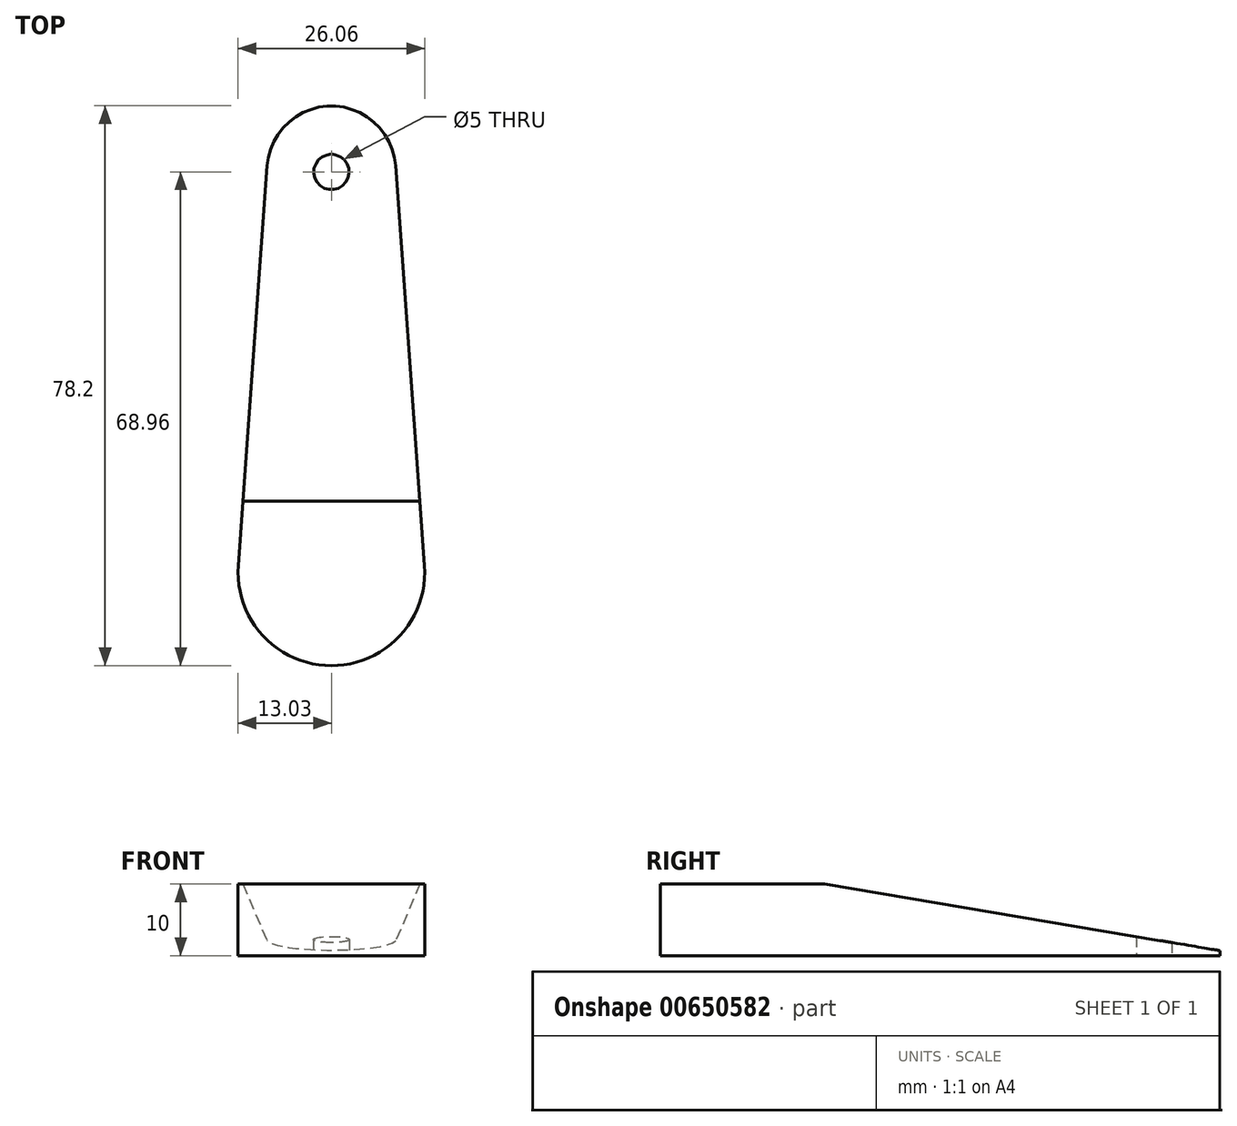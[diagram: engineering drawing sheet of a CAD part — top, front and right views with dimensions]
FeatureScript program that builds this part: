
annotation { "Feature Type Name" : "Feature", "Feature Type Description" : "" }
export const myFeature = defineFeature(function(context is Context, id is Id, definition is map)
    precondition{}
    {
        {
            var Q0;
            Q0=qCreatedBy(makeId("Top.planeOp"),FACE);
            var sketch = newSketch(context, id + "F0", { "sketchPlane" : qUnion([Q0])});
            skLineSegment(sketch, "E0", {"start": v(13, 0) * mm, "end": v(9, 55.86) * mm});
            skLineSegment(sketch, "E1", {"start": v(-13, 0) * mm, "end": v(-9, 55.86) * mm});
            skArc(sketch, "E2", {"start": v(-13, 0) * mm, "mid": v(0, -13.96) * mm, "end": v(13, 0) * mm});
            skArc(sketch, "E3", {"start": v(9, 55.86) * mm, "mid": v(0, 64.24) * mm, "end": v(-9, 55.86) * mm});
            skCircle(sketch, "E4", {"center": v(0, 55) * mm, "radius": 2.5 * mm});
            skPoint(sketch, "E5", {"position": v(0, 0) * mm});
            skSolve(sketch);
        }
        {
            var Q0;
            Q0 = qSketchRegion(id + "F0", true);
            extrude(context, id + "F1", {"entities" : qUnion([Q0]), "depth" : 10 * mm, "offsetDistance" : 25 * mm});
        }
        {
            var Q0;
            Q0=qCreatedBy(makeId("Right.planeOp"),FACE);
            var sketch = newSketch(context, id + "F2", { "sketchPlane" : qUnion([Q0])});
            skLineSegment(sketch, "E6", {"start": v(9, 10) * mm, "end": v(68.33, 0) * mm});
            skLineSegment(sketch, "E7", {"start": v(9, 10) * mm, "end": v(68.33, 10) * mm});
            skLineSegment(sketch, "E8", {"start": v(68.33, 0) * mm, "end": v(68.33, 10) * mm});
            skSolve(sketch);
        }
        {
            var Q0;
            Q0 = qSketchRegion(id + "F2", true);
            extrude(context, id + "F3", {"entities" : qUnion([Q0]), "operationType" : NewBodyOperationType.REMOVE, "endBound" : BoundingType.SYMMETRIC, "depth" : 50 * mm, "offsetDistance" : 25 * mm});
        }
    });
